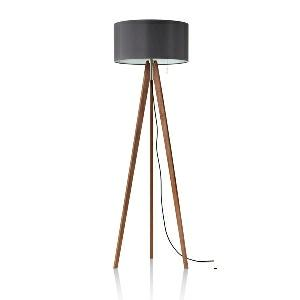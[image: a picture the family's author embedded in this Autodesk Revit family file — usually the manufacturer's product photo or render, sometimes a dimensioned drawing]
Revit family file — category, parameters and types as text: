
# Revit family: vivaa_free_-_vfs_7000_vtl_d_00812675_b569
name_source: partatom
category: Lighting Fixtures
units: mm (PartAtom-declared; Revit-internal decimal feet)

## family parameters
Cut with Voids When Loaded = No
Host = Face
Light Source = No
Part Type = Normal
Room Calculation Point = No
Round Connector Dimension = Use Diameter
Shared = No

## types (1)
- VIVAA.free - VFS 7000/VTL/D (1 x LED, 7200 lm, 2700-6500K)
    Apparent Load = 79 VA
    Approval mark = CE
    CIE Flux Codes = 52 82 95 44 100
    Color Rendering = 90-100
    Color Temperature = 2700-6500K
    Control Gear = Electronic ballast
    Default Elevation = 1800 mm
    Description = VFS 7000/VTL/D|Free-standing luminaire|light source:   Daylight   |work equipment: Electronic ballast|luminous flux: 7200 lm|light distribution: Direct/indirect|direct ratio: approx. 44 %|color rendering index (CRI): >= 90|chromaticity tolerance:  3 SDCM|technology: Continuously dimmable|operation: Pull cord|luminaire body|material: Polyethylene(PE)|surface: Untreated|colour: Anthracite|lamp cover: Polycarbonate (PC), Satine|tubular section|material: Wood|surface: Stained|Form: Tubular section upright|colour of tubular section: Ash dark|weight (net): approx. 6.4 kg|mains lead: 3.40 m Mains plug CEE 7/VII|Fastening: Floor standing base|glare control: Diffusor|luminance(L65): <= 1600 cd/m|unified glare rating(4H 8H): <=  16|special features: App control, Biodynamic light VTL|
    Frequency = 50 Hz, 60 Hz
    Height = 250 mm
    Lamp = 1 x LED
    Lamp Light Flux = 7200 lm
    Lamp count = 1
    Length = 520 mm
    Luminous efficacy = 91 lm/W
    Manufacturer = Waldmann
    ModVariant = No
    Model = 00812675
    Mounting Place = Floor
    Mounting Type = Freestanding
    Number of Poles = 1
    OnlyDefault = Yes
    Power Factor = 1
    Product Name = VIVAA.free - VFS 7000/VTL/D
    Product group = Free standing luminaire
    ProductGroupID = 13
    Protection Class = Protection class I
    Protection Degree = Degree of protection
    RLX_Detail_Level = 1
    RLX_Emergency_Light_Flux = 0 lm
    RLX_Emergency_Type = 0
    RLX_Emergency_Type_DB = No
    RlxData = <blob elided: 29557 chars, md5=6df3e886>
    Socket = socket
    Standby Power = 0 W
    System Light Flux = 7200 lm
    System Power = 79 W
    Type Comments = Product without accessories
    Type Image = vivaa_free_wood_rgb.jpg
    URL = http://relux.com
    VarID = ---
    Voltage = 230 V
    Voltage Range = 220-240 V
    Weight = 0.00 kg
    Width = 0 mm  [stored 0 ft]

note: [stored X ft] marks values corroborated as IEEE doubles in the binary element streams (Revit-internal decimal feet)

## geometry (parser evidence)
native form markers: Blend x4, Sweep x14
no freeform markers — native parametric forms only
